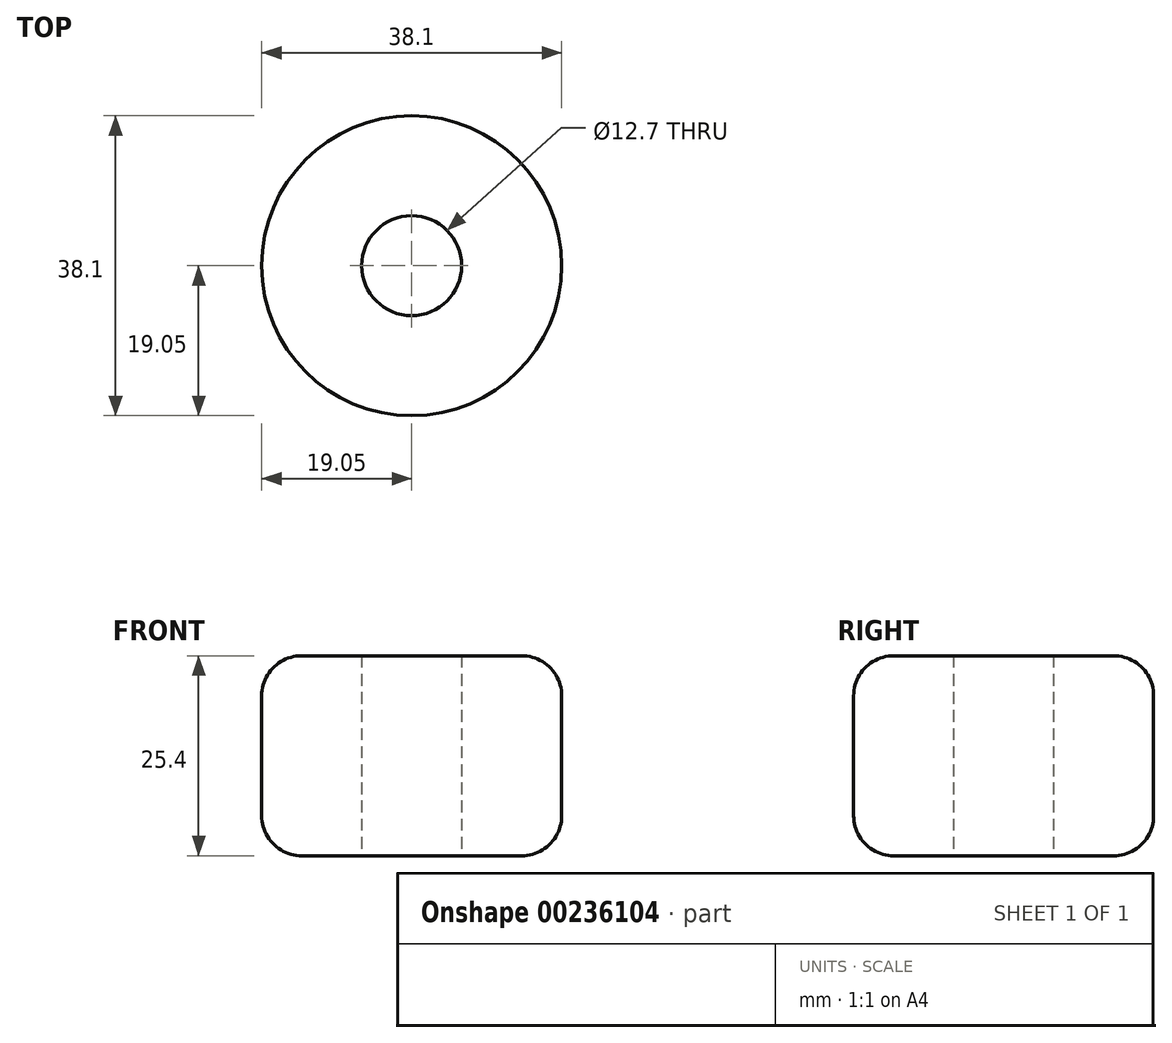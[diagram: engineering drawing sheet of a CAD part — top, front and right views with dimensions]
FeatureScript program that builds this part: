
annotation { "Feature Type Name" : "Feature", "Feature Type Description" : "" }
export const myFeature = defineFeature(function(context is Context, id is Id, definition is map)
    precondition{}
    {
        {
            var Q0;
            Q0=qCreatedBy(makeId("Top.planeOp"),FACE);
            var sketch = newSketch(context, id + "F0", { "sketchPlane" : qUnion([Q0])});
            skCircle(sketch, "E0", {"center": v(0, 0) * mm, "radius": 19.05 * mm});
            skCircle(sketch, "E1", {"center": v(0, 0) * mm, "radius": 6.35 * mm});
            skSolve(sketch);
        }
        {
            var Q0;
            Q0 = qSketchRegion(id + "F0", true);
            extrude(context, id + "F1", {"entities" : qUnion([Q0]), "endBound" : BoundingType.SYMMETRIC, "depth" : 25.4 * mm});
        }
        {
            var Q0;
            Q0=makeQuery(id+"F1.opExtrude","CAP_EDGE",EDGE,{"disambiguationData":[OSD([sQuery(id+"F0.wireOp",EDGE,"E0")])],"isStart":true});
            var Q1;
            Q1=makeQuery(id+"F1.opExtrude","CAP_EDGE",EDGE,{"disambiguationData":[OSD([sQuery(id+"F0.wireOp",EDGE,"E0")])],"isStart":false});
            fillet(context, id + "F2", {"entities" : qUnion([Q0, Q1]), "radius" : 5.08 * mm, "tangentPropagation" : true, "allowEdgeOverflow" : false});
        }
        {
            var Q0;
            Q0 = qSketchRegion(id + "F0", true);
            extrude(context, id + "F3", {"entities" : qUnion([Q0]), "operationType" : NewBodyOperationType.ADD, "endBound" : BoundingType.SYMMETRIC, "depth" : 25.4 * mm});
        }
        {
            var Q0;
            Q0=makeQuery(id+"F3.opExtrude","CAP_EDGE",EDGE,{"disambiguationData":[OSD([sQuery(id+"F0.wireOp",EDGE,"E0")])],"isStart":true});
            var Q1;
            Q1=makeQuery(id+"F3.opExtrude","CAP_EDGE",EDGE,{"disambiguationData":[OSD([sQuery(id+"F0.wireOp",EDGE,"E0")])],"isStart":false});
            fillet(context, id + "F4", {"entities" : qUnion([Q0, Q1]), "radius" : 5.08 * mm, "tangentPropagation" : true, "allowEdgeOverflow" : false});
        }
    });
